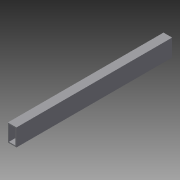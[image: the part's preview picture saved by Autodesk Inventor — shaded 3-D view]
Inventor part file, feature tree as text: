
AUTODESK INVENTOR PART (.ipt)
format: ipt  version: 2015 (Build 190159000, 159)  size: 74,240 bytes
history: native  units: in
note: dims shown in document units (in); Inventor stores cm internally (conversion verified against a paired STEP export)
features: extrude x1, sketch x1
ambient origin geometry x8: Origin, YZ Plane, XZ Plane, XY Plane, X Axis, Y Axis, Z Axis, Center Point
bodies: Solid1 (feature_tree)
feature tree (2):
  extrude  "Extrusion1"  Depth=18.0in TaperAngle=0.0deg
  sketch  "Sketch1"  dims[d0=1.0in d1=2.0in d2=0.125in d3=18.0in d4=0.0in]
